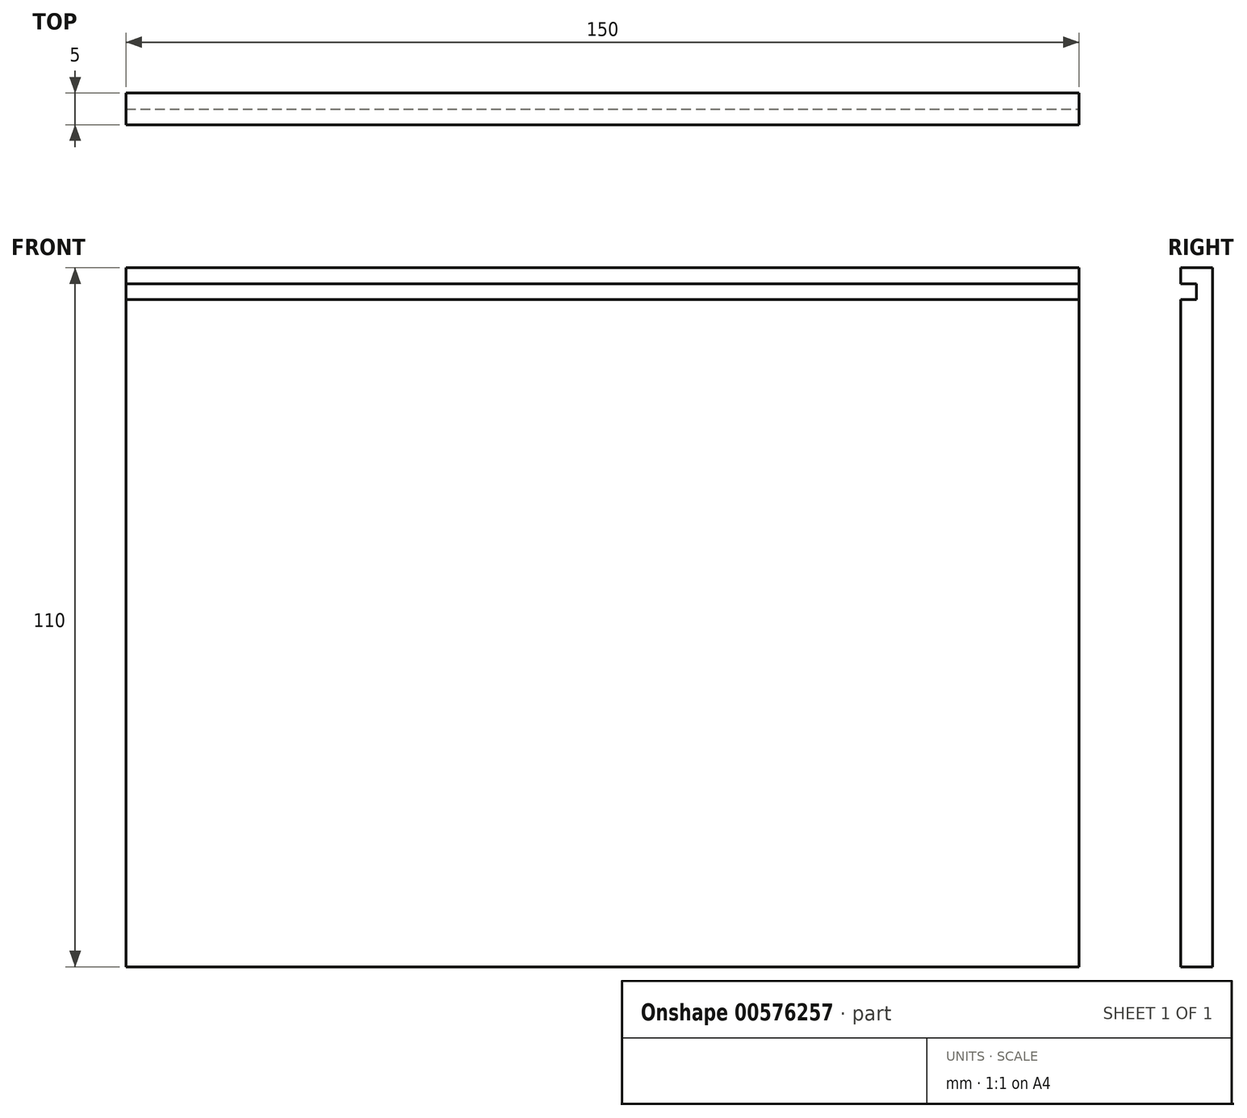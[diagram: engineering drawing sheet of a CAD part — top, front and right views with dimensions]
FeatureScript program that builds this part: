
annotation { "Feature Type Name" : "Feature", "Feature Type Description" : "" }
export const myFeature = defineFeature(function(context is Context, id is Id, definition is map)
    precondition{}
    {
        {
            var Q0;
            Q0=qCreatedBy(makeId("Front.planeOp"),FACE);
            var sketch = newSketch(context, id + "F0", { "sketchPlane" : qUnion([Q0])});
            skLineSegment(sketch, "E0.bottom", {"start": v(75, -52.5) * mm, "end": v(-75, -52.5) * mm});
            skLineSegment(sketch, "E0.left", {"start": v(75, -52.5) * mm, "end": v(75, 52.5) * mm});
            skLineSegment(sketch, "E0.right", {"start": v(-75, -52.5) * mm, "end": v(-75, 52.5) * mm});
            skPoint(sketch, "E0.middle", {"position": v(0, 0) * mm});
            skLineSegment(sketch, "E1", {"start": v(-75, 52.5) * mm, "end": v(-75, 57.5) * mm});
            skLineSegment(sketch, "E2", {"start": v(-75, 57.5) * mm, "end": v(75, 57.5) * mm});
            skLineSegment(sketch, "E3", {"start": v(75, 57.5) * mm, "end": v(75, 52.5) * mm});
            skSolve(sketch);
        }
        {
            var Q0;
            Q0=qSketchRegion(id+"F0",true);
            extrude(context, id + "F1", {"entities" : qUnion([Q0]), "depth" : 5 * mm, "offsetDistance" : 25 * mm});
        }
        {
            var Q0;
            Q0=makeQuery(id+"F1.opExtrude","CAP_FACE",FACE,{"disambiguationData":[OSD([sQuery(id+"F0.wireOp",EDGE,"E0.bottom"),sQuery(id+"F0.wireOp",EDGE,"E0.left"),sQuery(id+"F0.wireOp",EDGE,"E0.right"),sQuery(id+"F0.wireOp",EDGE,"E1"),sQuery(id+"F0.wireOp",EDGE,"E2"),sQuery(id+"F0.wireOp",EDGE,"E3")])],"isStart":false});
            var sketch = newSketch(context, id + "F2", { "sketchPlane" : qUnion([Q0])});
            skLineSegment(sketch, "E4", {"start": v(-75, 55) * mm, "end": v(-75, 52.5) * mm});
            skLineSegment(sketch, "E5", {"start": v(-75, 52.5) * mm, "end": v(75, 52.5) * mm});
            skLineSegment(sketch, "E6", {"start": v(-75, 55) * mm, "end": v(75, 55) * mm});
            skSolve(sketch);
        }
        {
            var Q0;
            Q0=makeQuery(id+"F2.imprint","IMPRINT",FACE,{"disambiguationData":[TD([[makeQuery(id+"F2.imprint","IMPRINT",EDGE,{"derivedFrom":sQuery(id+"F2.wireOp",EDGE,"E4")}),-1.0]])]});
            extrude(context, id + "F3", {"entities" : qUnion([Q0]), "operationType" : NewBodyOperationType.REMOVE, "oppositeDirection" : true, "depth" : 2.5 * mm, "offsetDistance" : 25 * mm});
        }
    });
